# Revit family: Поли-Групп_КлапанОбратныйEAZ-RTS_DN50-600
name_source: partatom
category: Арматура трубопроводов
units: mm (PartAtom-declared; Revit-internal decimal feet)

## family parameters
Всегда вертикально = Да
На основе рабочей плоскости = Нет
Общий = Нет
При загрузке вырезать с полостями = Нет
Размер круглого соединителя = Использовать диаметр
Тип детали = Нормальный

## types (28) — shared parameters
ADSK_URL страницы изделия = https://www.polycorr.ru
ADSK_Версия Revit = 2019
ADSK_Единица измерения = шт.
ADSK_Завод-изготовитель = ООО ПК Поли-Групп
ADSK_Количество = 1
ADSK_Материал = ВЧШГ GGG50 синий
ADSK_Материал наименование = Высокопрочный чугун с шаровидным графитом (GGG-40)
ADSK_Потеря давления жидкости = 0.0 бары
ADSK_Расход жидкости = 0.0 м³/ч
Класс герметичности = А по ГОСТ Р 9544-2015
Материал диска = Высокотемпературная углеродистая сталь
Материал диска/шара/створки = Сталь высокотемпературная углеродистая
Материал уплотнителя = EPDM
Назначение = Для предотвращения обратного потока среды на трубопроводах
Покрытие = Высококачественное эпоксидное покрытие толщиной 300 мкм
Рабочая среда = Питьевая вода, техническая вода, канализационные стоки, морская вода.
Разработчик = https://3dbim.pro
Срок службы = 50 лет
ТВ = КлапанОбратныйEAZ-RTS_DN50-600_Поли-Групп
Температура рабочей среды = 0 до +70°С
Тип привода = Без привода
Тип присоединения = Фланцевое

## per-type parameters (varying)
| type | ADSK_Диаметр условный | ADSK_Марка | ADSK_Масса | ADSK_Масса_Текст | ADSK_Наименование | ADSK_Наименование краткое | D | D2 | DN | H | Kv | L | PN | a2 | b | d | d2 | d4 | f | l1 | l2 | Габаритные размеры |
| 50-10 | 50 мм | EAZ-DCh-1 DN50 PN10 | 8.5 | 8.5 | Клапан обратный EAZ RTS дисковый фланцевый DN50 PN10 | Клапан обратный EAZ RTS DN50 PN10 | 165 мм | 100 мм | 50 мм | 88 мм | 0.6 м³/ч | 200 мм | 10.0 бары | 100 мм | 19 мм | 60 мм | 50 мм | 55 мм | 3 мм | 25 мм | 40 мм | 165х88х200 |
| 65-10 | 65 мм | EAZ-DCh-1 DN65 PN10 | 12 | 12 | Клапан обратный EAZ RTS дисковый фланцевый DN65 PN10 | Клапан обратный EAZ RTS DN65 PN10 | 185 мм | 120 мм | 65 мм | 94 мм | 0.6 м³/ч | 240 мм | 10.0 бары | 120 мм | 19 мм | 78 мм | 65 мм | 72 мм | 3 мм | 25 мм | 40 мм | 185х94х240 |
| 80-10 | 80 мм | EAZ-DCh-1 DN80 PN10 | 14.4 | 14.4 | Клапан обратный EAZ RTS дисковый фланцевый DN80 PN10 | Клапан обратный EAZ RTS DN80 PN10 | 200 мм | 135 мм | 80 мм | 110 мм | 0.6 м³/ч | 260 мм | 10.0 бары | 130 мм | 19 мм | 96 мм | 80 мм | 88 мм | 3 мм | 25 мм | 48 мм | 200х110х260 |
| 100-10 | 100 мм | EAZ-DCh-1 DN100 PN10 | 19 | 19 | Клапан обратный EAZ RTS дисковый фланцевый DN100 PN10 | Клапан обратный EAZ RTS DN100 PN10 | 220 мм | 156 мм | 100 мм | 115 мм | 0.6 м³/ч | 300 мм | 10.0 бары | 150 мм | 19 мм | 120 мм | 100 мм | 110 мм | 3 мм | 40 мм | 52 мм | 220х115х300 |
| 125-10 | 125 мм | EAZ-DCh-1 DN125 PN10 | 28 | 28 | Клапан обратный EAZ RTS дисковый фланцевый DN125 PN10 | Клапан обратный EAZ RTS DN125 PN10 | 250 мм | 186 мм | 125 мм | 165 мм | 0.6 м³/ч | 350 мм | 10.0 бары | 175 мм | 19 мм | 150 мм | 125 мм | 138 мм | 3 мм | 40 мм | 60 мм | 250х165х350 |
| 150-10 | 150 мм | EAZ-DCh-1 DN150 PN10 | 33.5 | 33.5 | Клапан обратный EAZ RTS дисковый фланцевый DN150 PN10 | Клапан обратный EAZ RTS DN150 PN10 | 285 мм | 212 мм | 150 мм | 170 мм | 0.6 м³/ч | 400 мм | 10.0 бары | 200 мм | 19 мм | 180 мм | 150 мм | 165 мм | 3 мм | 40 мм | 80 мм | 285х170х400 |
| 200-10 | 200 мм | EAZ-DCh-1 DN200 PN10 | 68.5 | 68.5 | Клапан обратный EAZ RTS дисковый фланцевый DN200 PN10 | Клапан обратный EAZ RTS DN200 PN10 | 340 мм | 268 мм | 200 мм | 224 мм | 0.6 м³/ч | 500 мм | 10.0 бары | 250 мм | 20 мм | 240 мм | 200 мм | 220 мм | 3 мм | 40 мм | 110 мм | 340х224х500 |
| 250-10 | 250 мм | EAZ-DCh-1 DN250 PN10 | 120 | 120 | Клапан обратный EAZ RTS дисковый фланцевый DN250 PN10 | Клапан обратный EAZ RTS DN250 PN10 | 405 мм | 318 мм | 250 мм | 261 мм | 0.6 м³/ч | 600 мм | 10.0 бары | 300 мм | 22 мм | 300 мм | 250 мм | 275 мм | 3 мм | 40 мм | 130 мм | 405х261х600 |
| 300-10 | 300 мм | EAZ-DCh-1 DN300 PN10 | 160 | 160 | Клапан обратный EAZ RTS дисковый фланцевый DN300 PN10 | Клапан обратный EAZ RTS DN300 PN10 | 460 мм | 370 мм | 300 мм | 310 мм | 0.6 м³/ч | 700 мм | 10.0 бары | 350 мм | 25 мм | 360 мм | 300 мм | 330 мм | 3 мм | 80 мм | 170 мм | 460х310х700 |
| 350-10 | 350 мм | EAZ-DCh-1 DN350 PN10 | 250 | 250 | Клапан обратный EAZ RTS дисковый фланцевый DN350 PN10 | Клапан обратный EAZ RTS DN350 PN10 | 520 мм | 430 мм | 350 мм | 320 мм | 0.6 м³/ч | 800 мм | 10.0 бары | 400 мм | 27 мм | 420 мм | 350 мм | 385 мм | 3 мм | 80 мм | 200 мм | 520х320х800 |
| 400-10 | 400 мм | EAZ-DCh-1 DN400 PN10 | 293 | 293 | Клапан обратный EAZ RTS дисковый фланцевый DN400 PN10 | Клапан обратный EAZ RTS DN400 PN10 | 580 мм | 480 мм | 400 мм | 380 мм | 0.6 м³/ч | 900 мм | 10.0 бары | 450 мм | 28 мм | 480 мм | 400 мм | 440 мм | 3 мм | 80 мм | 220 мм | 580х380х900 |
| 450-10 | 450 мм | EAZ-DCh-1 DN450 PN10 | 513 | 513 | Клапан обратный EAZ RTS дисковый фланцевый DN450 PN10 | Клапан обратный EAZ RTS DN450 PN10 | 640 мм | 528 мм | 450 мм | 455 мм | 0.6 м³/ч | 965 мм | 10.0 бары | 483 мм | 30 мм | 540 мм | 450 мм | 495 мм | 4 мм | 80 мм | 280 мм | 640х455х965 |
| 500-10 | 500 мм | EAZ-DCh-1 DN500 PN10 | 809 | 809 | Клапан обратный EAZ RTS дисковый фланцевый DN500 PN10 | Клапан обратный EAZ RTS DN500 PN10 | 715 мм | 582 мм | 500 мм | 470 мм | 0.6 м³/ч | 1067 мм | 10.0 бары | 534 мм | 32 мм | 600 мм | 500 мм | 550 мм | 4 мм | 80 мм | 330 мм | 715х470х1067 |
| 600-10 | 600 мм | EAZ-DCh-1 DN600 PN10 | 1130 | 1130 | Клапан обратный EAZ RTS дисковый фланцевый DN600 PN10 | Клапан обратный EAZ RTS DN600 PN10 | 840 мм | 680 мм | 600 мм | 550 мм | 0.6 м³/ч | 1295 мм | 10.0 бары | 648 мм | 36 мм | 720 мм | 600 мм | 660 мм | 4 мм | 80 мм | 380 мм | 840х550х1295 |
| 50-16 | 50 мм | EAZ-DCh-1 DN50 PN16 | 8.5 | 8.5 | Клапан обратный EAZ RTS дисковый фланцевый DN50 PN16 | Клапан обратный EAZ RTS DN50 PN16 | 165 мм | 100 мм | 50 мм | 88 мм | 0.5 м³/ч | 200 мм | 16.0 бары | 100 мм | 19 мм | 60 мм | 50 мм | 55 мм | 3 мм | 25 мм | 40 мм | 165х88х200 |
| 65-16 | 65 мм | EAZ-DCh-1 DN65 PN16 | 12 | 12 | Клапан обратный EAZ RTS дисковый фланцевый DN65 PN16 | Клапан обратный EAZ RTS DN65 PN16 | 185 мм | 120 мм | 65 мм | 94 мм | 0.5 м³/ч | 240 мм | 16.0 бары | 120 мм | 19 мм | 78 мм | 65 мм | 72 мм | 3 мм | 25 мм | 40 мм | 185х94х240 |
| 80-16 | 80 мм | EAZ-DCh-1 DN80 PN16 | 14.4 | 14.4 | Клапан обратный EAZ RTS дисковый фланцевый DN80 PN16 | Клапан обратный EAZ RTS DN80 PN16 | 200 мм | 135 мм | 80 мм | 110 мм | 0.5 м³/ч | 260 мм | 16.0 бары | 130 мм | 19 мм | 96 мм | 80 мм | 88 мм | 3 мм | 25 мм | 48 мм | 200х110х260 |
| 100-16 | 100 мм | EAZ-DCh-1 DN100 PN16 | 19 | 19 | Клапан обратный EAZ RTS дисковый фланцевый DN100 PN16 | Клапан обратный EAZ RTS DN100 PN16 | 220 мм | 156 мм | 100 мм | 115 мм | 0.5 м³/ч | 300 мм | 16.0 бары | 150 мм | 19 мм | 120 мм | 100 мм | 110 мм | 3 мм | 40 мм | 52 мм | 220х115х300 |
| 125-16 | 125 мм | EAZ-DCh-1 DN125 PN16 | 28 | 28 | Клапан обратный EAZ RTS дисковый фланцевый DN125 PN16 | Клапан обратный EAZ RTS DN125 PN16 | 250 мм | 186 мм | 125 мм | 165 мм | 0.5 м³/ч | 350 мм | 16.0 бары | 175 мм | 19 мм | 150 мм | 125 мм | 138 мм | 3 мм | 40 мм | 60 мм | 250х165х350 |
| 150-16 | 150 мм | EAZ-DCh-1 DN150 PN16 | 33.5 | 33.5 | Клапан обратный EAZ RTS дисковый фланцевый DN150 PN16 | Клапан обратный EAZ RTS DN150 PN16 | 285 мм | 212 мм | 150 мм | 170 мм | 0.5 м³/ч | 400 мм | 16.0 бары | 200 мм | 19 мм | 180 мм | 150 мм | 165 мм | 3 мм | 40 мм | 80 мм | 285х170х400 |
| 200-16 | 200 мм | EAZ-DCh-1 DN200 PN16 | 68.5 | 68.5 | Клапан обратный EAZ RTS дисковый фланцевый DN200 PN16 | Клапан обратный EAZ RTS DN200 PN16 | 340 мм | 268 мм | 200 мм | 224 мм | 0.5 м³/ч | 500 мм | 16.0 бары | 250 мм | 20 мм | 240 мм | 200 мм | 220 мм | 3 мм | 40 мм | 110 мм | 340х224х500 |
| 250-16 | 250 мм | EAZ-DCh-1 DN250 PN16 | 120 | 120 | Клапан обратный EAZ RTS дисковый фланцевый DN250 PN16 | Клапан обратный EAZ RTS DN250 PN16 | 405 мм | 318 мм | 250 мм | 261 мм | 0.5 м³/ч | 600 мм | 16.0 бары | 300 мм | 22 мм | 300 мм | 250 мм | 275 мм | 3 мм | 40 мм | 130 мм | 405х261х600 |
| 300-16 | 300 мм | EAZ-DCh-1 DN300 PN16 | 160 | 160 | Клапан обратный EAZ RTS дисковый фланцевый DN300 PN16 | Клапан обратный EAZ RTS DN300 PN16 | 460 мм | 373 мм | 300 мм | 310 мм | 0.5 м³/ч | 700 мм | 16.0 бары | 350 мм | 25 мм | 360 мм | 300 мм | 330 мм | 3 мм | 80 мм | 170 мм | 460х310х700 |
| 350-16 | 350 мм | EAZ-DCh-1 DN350 PN16 | 250 | 250 | Клапан обратный EAZ RTS дисковый фланцевый DN350 PN16 | Клапан обратный EAZ RTS DN350 PN16 | 520 мм | 433 мм | 350 мм | 320 мм | 0.5 м³/ч | 800 мм | 16.0 бары | 400 мм | 27 мм | 420 мм | 350 мм | 385 мм | 3 мм | 80 мм | 200 мм | 520х320х800 |
| 400-16 | 400 мм | EAZ-DCh-1 DN400 PN16 | 293 | 293 | Клапан обратный EAZ RTS дисковый фланцевый DN400 PN16 | Клапан обратный EAZ RTS DN400 PN16 | 580 мм | 483 мм | 400 мм | 380 мм | 0.5 м³/ч | 900 мм | 16.0 бары | 450 мм | 28 мм | 480 мм | 400 мм | 440 мм | 3 мм | 80 мм | 220 мм | 580х380х900 |
| 450-16 | 450 мм | EAZ-DCh-1 DN450 PN16 | 513 | 513 | Клапан обратный EAZ RTS дисковый фланцевый DN450 PN16 | Клапан обратный EAZ RTS DN450 PN16 | 640 мм | 546 мм | 450 мм | 455 мм | 0.5 м³/ч | 965 мм | 16.0 бары | 483 мм | 30 мм | 540 мм | 450 мм | 495 мм | 4 мм | 80 мм | 280 мм | 640х455х965 |
| 500-16 | 500 мм | EAZ-DCh-1 DN500 PN16 | 809 | 809 | Клапан обратный EAZ RTS дисковый фланцевый DN500 PN16 | Клапан обратный EAZ RTS DN500 PN16 | 715 мм | 605 мм | 500 мм | 470 мм | 0.5 м³/ч | 1067 мм | 16.0 бары | 534 мм | 32 мм | 600 мм | 500 мм | 550 мм | 4 мм | 80 мм | 330 мм | 715х470х1067 |
| 600-16 | 600 мм | EAZ-DCh-1 DN600 PN16 | 1130 | 1130 | Клапан обратный EAZ RTS дисковый фланцевый DN600 PN16 | Клапан обратный EAZ RTS DN600 PN16 | 840 мм | 720 мм | 600 мм | 550 мм | 0.5 м³/ч | 1295 мм | 16.0 бары | 648 мм | 36 мм | 720 мм | 600 мм | 660 мм | 4 мм | 80 мм | 380 мм | 840х550х1295 |
